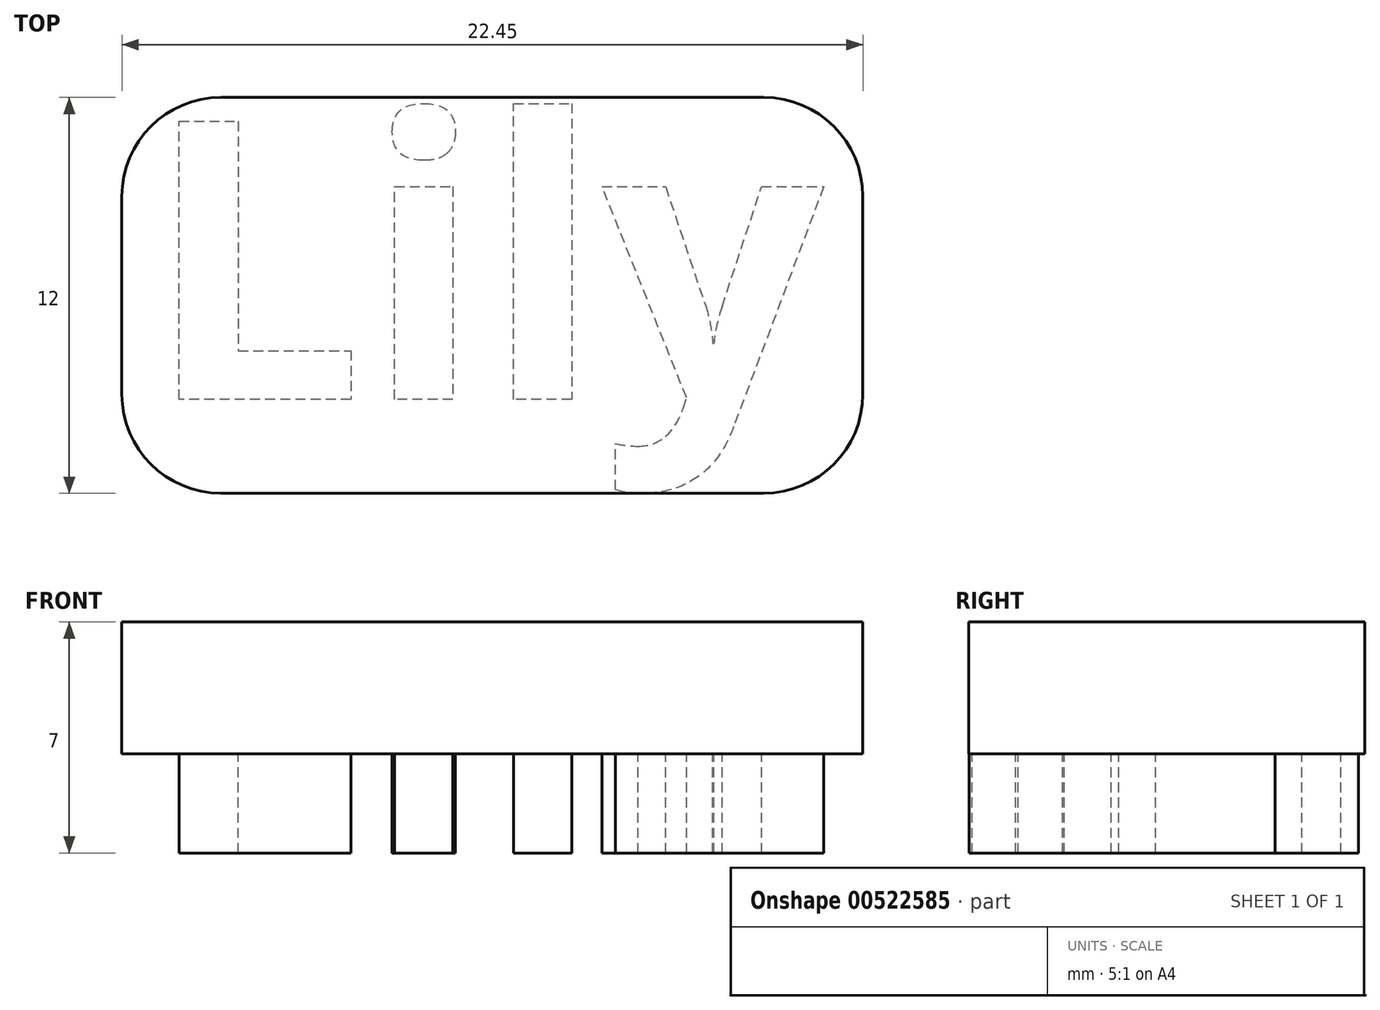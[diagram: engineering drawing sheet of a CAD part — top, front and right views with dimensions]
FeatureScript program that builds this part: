
annotation { "Feature Type Name" : "Feature", "Feature Type Description" : "" }
export const myFeature = defineFeature(function(context is Context, id is Id, definition is map)
    precondition{}
    {
        {
            var Q0;
            Q0=qCreatedBy(makeId("Top.planeOp"),FACE);
            var sketch = newSketch(context, id + "F0", { "sketchPlane" : qUnion([Q0])});
            skText(sketch, "E0", { "text": "Lily", "fontName": "OpenSans-Bold.ttf"});
            skPoint(sketch, "E1", {"position": v(0, 0) * mm});
            const initialGuessF0  = {"E0": [-0.01068, -0.00425, 1, 0, 0.0085]};
            skSetInitialGuess(sketch, initialGuessF0);
            skSolve(sketch);
        }
        {
            var Q0;
            Q0=qCreatedBy(makeId("Top.planeOp"),FACE);
            var sketch = newSketch(context, id + "F1", { "sketchPlane" : qUnion([Q0])});
            skLineSegment(sketch, "E2.bottom", {"start": v(-11.35, 4.9) * mm, "end": v(11.1, 4.9) * mm});
            skLineSegment(sketch, "E2.top", {"start": v(-11.35, -7.1) * mm, "end": v(11.1, -7.1) * mm});
            skLineSegment(sketch, "E2.left", {"start": v(-11.35, 4.9) * mm, "end": v(-11.35, -7.1) * mm});
            skLineSegment(sketch, "E2.right", {"start": v(11.1, 4.9) * mm, "end": v(11.1, -7.1) * mm});
            skSolve(sketch);
        }
        {
            var Q0;
            Q0=makeQuery(id+"F1.imprint","IMPRINT",FACE,{"disambiguationData":[TD([[makeQuery(id+"F1.imprint","IMPRINT",EDGE,{"derivedFrom":sQuery(id+"F1.wireOp",EDGE,"E2.bottom")}),-1.0]])]});
            extrude(context, id + "F2", {"entities" : qUnion([Q0]), "depth" : 4 * mm, "offsetDistance" : 25 * mm});
        }
        {
            var Q0;
            Q0 = qSketchRegion(id + "F0", true);
            extrude(context, id + "F3", {"entities" : qUnion([Q0]), "operationType" : NewBodyOperationType.ADD, "oppositeDirection" : true, "depth" : 3 * mm, "offsetDistance" : 25 * mm});
        }
        {
            var Q0;
            Q0=makeQuery(id+"F2.opExtrude","SWEPT_EDGE",EDGE,{"disambiguationData":[OSD([sQuery(id+"F1.wireOp",EDGE,"E2.bottom"),sQuery(id+"F1.wireOp",EDGE,"E2.right")])]});
            var Q1;
            Q1=makeQuery(id+"F2.opExtrude","SWEPT_EDGE",EDGE,{"disambiguationData":[OSD([sQuery(id+"F1.wireOp",EDGE,"E2.bottom"),sQuery(id+"F1.wireOp",EDGE,"E2.left")])]});
            var Q2;
            Q2=makeQuery(id+"F2.opExtrude","SWEPT_EDGE",EDGE,{"disambiguationData":[OSD([sQuery(id+"F1.wireOp",EDGE,"E2.top"),sQuery(id+"F1.wireOp",EDGE,"E2.right")])]});
            var Q3;
            Q3=makeQuery(id+"F2.opExtrude","SWEPT_EDGE",EDGE,{"disambiguationData":[OSD([sQuery(id+"F1.wireOp",EDGE,"E2.top"),sQuery(id+"F1.wireOp",EDGE,"E2.left")])]});
            fillet(context, id + "F4", {"entities" : qUnion([Q0, Q1, Q2, Q3]), "radius" : 3 * mm, "tangentPropagation" : true, "allowEdgeOverflow" : false});
        }
    });
